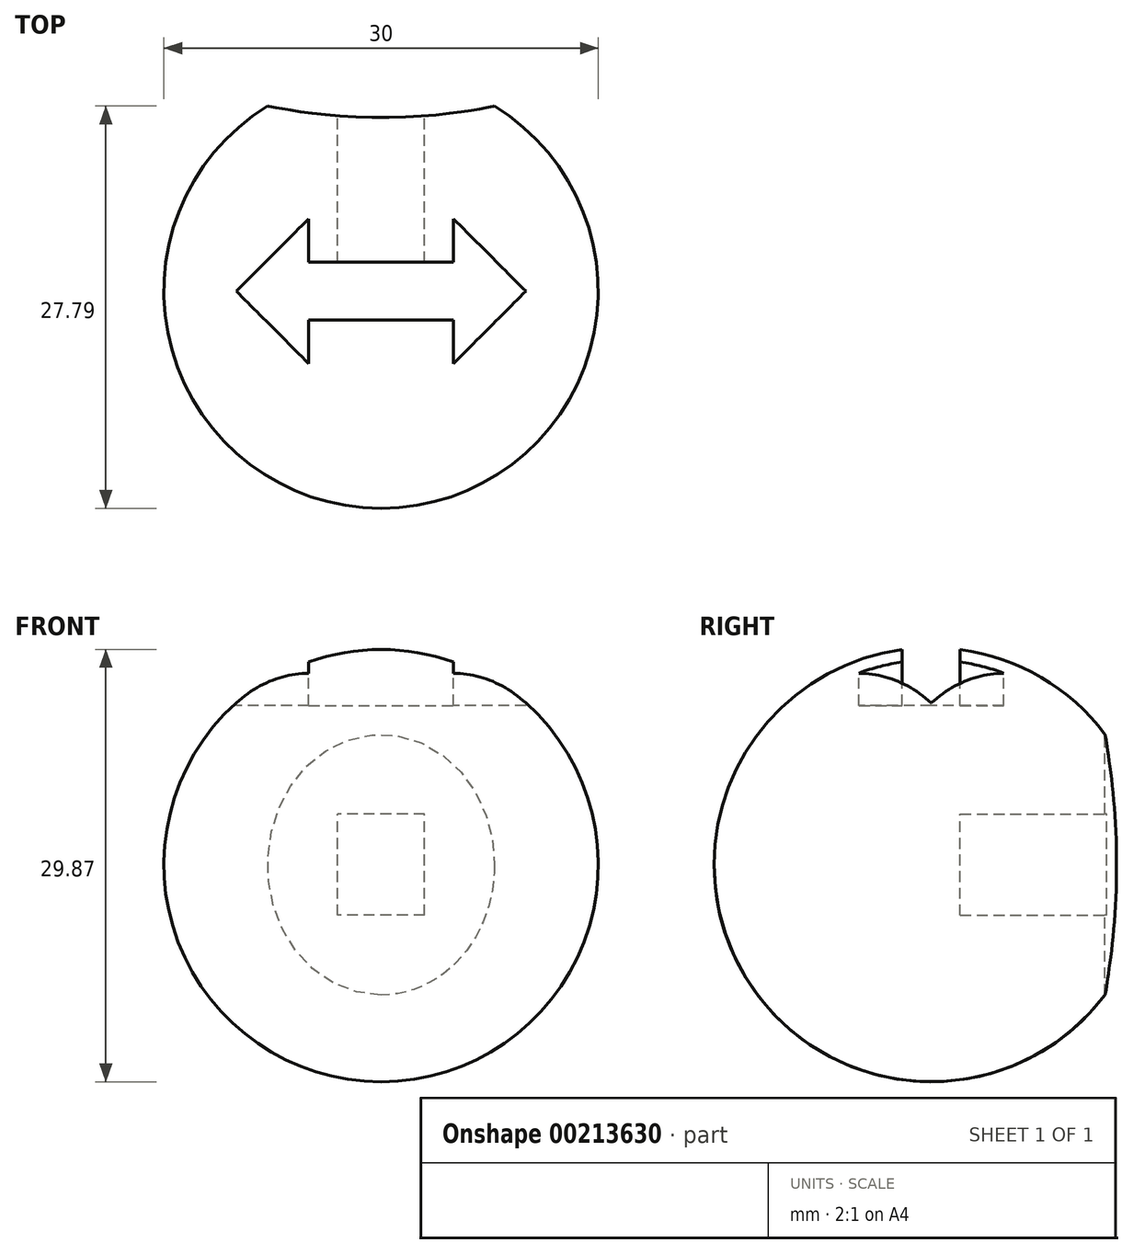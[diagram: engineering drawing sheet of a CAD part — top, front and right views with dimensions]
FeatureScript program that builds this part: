
annotation { "Feature Type Name" : "Feature", "Feature Type Description" : "" }
export const myFeature = defineFeature(function(context is Context, id is Id, definition is map)
    precondition{}
    {
        {
            var Q0;
            Q0=qCreatedBy(makeId("Right.planeOp"),FACE);
            var sketch = newSketch(context, id + "F0", { "sketchPlane" : qUnion([Q0])});
            skLineSegment(sketch, "E0", {"start": v(0, 0) * mm, "end": v(-30, 0) * mm});
            skArc(sketch, "E1", {"start": v(0, 0) * mm, "mid": v(-15, 15) * mm, "end": v(-30, 0) * mm});
            skSolve(sketch);
        }
        {
            var Q0;
            Q0=qSketchRegion(id+"F0",true);
            var Q1;
            Q1=sQuery(id+"F0.wireOp",EDGE,"E0");
            revolve(context, id + "F1", {"entities" : qUnion([Q0]), "axis" : qUnion([Q1]), "revolveType" : RevolveType.FULL});
        }
        {
            var Q0;
            Q0=qCreatedBy(makeId("Top.planeOp"),FACE);
            cPlane(context, id + "F2", {"entities" : qUnion([Q0]), "cplaneType" : CPlaneType.OFFSET, "offset" : 15 * mm, "width" : 150 * mm, "height" : 150 * mm});
        }
        {
            var Q0;
            Q0=qCreatedBy(id+"F2.planeOp",FACE);
            var sketch = newSketch(context, id + "F3", { "sketchPlane" : qUnion([Q0])});
            skLineSegment(sketch, "E2", {"start": v(0, 0) * mm, "end": v(0, -16.03) * mm, "construction": true});
            skLineSegment(sketch, "E3", {"start": v(0, 0) * mm, "end": v(-15, 0) * mm});
            skLineSegment(sketch, "E4", {"start": v(0, 0) * mm, "end": v(15, 0) * mm});
            skArc(sketch, "E5", {"start": v(-15, 0) * mm, "mid": v(0, -3) * mm, "end": v(15, 0) * mm});
            skSolve(sketch);
        }
        {
            var Q0;
            Q0=qSketchRegion(id+"F3",true);
            extrude(context, id + "F4", {"entities" : qUnion([Q0]), "operationType" : NewBodyOperationType.REMOVE, "endBound" : BoundingType.THROUGH_ALL, "oppositeDirection" : true, "depth" : 25 * mm});
        }
        {
            var Q0;
            Q0=qCreatedBy(makeId("Front.planeOp"),FACE);
            var sketch = newSketch(context, id + "F5", { "sketchPlane" : qUnion([Q0])});
            skLineSegment(sketch, "E6.bottom", {"start": v(3, -3.5) * mm, "end": v(-3, -3.5) * mm});
            skLineSegment(sketch, "E6.top", {"start": v(3, 3.5) * mm, "end": v(-3, 3.5) * mm});
            skLineSegment(sketch, "E6.left", {"start": v(3, -3.5) * mm, "end": v(3, 3.5) * mm});
            skLineSegment(sketch, "E6.right", {"start": v(-3, -3.5) * mm, "end": v(-3, 3.5) * mm});
            skPoint(sketch, "E6.middle", {"position": v(0, 0) * mm});
            skSolve(sketch);
        }
        {
            var Q0;
            Q0=qSketchRegion(id+"F5",true);
            extrude(context, id + "F6", {"entities" : qUnion([Q0]), "operationType" : NewBodyOperationType.REMOVE, "depth" : 13 * mm});
        }
        {
            var Q0;
            Q0=qCreatedBy(makeId("Top.planeOp"),FACE);
            cPlane(context, id + "F7", {"entities" : qUnion([Q0]), "cplaneType" : CPlaneType.OFFSET, "offset" : 18 * mm, "width" : 150 * mm, "height" : 150 * mm});
        }
        {
            var Q0;
            Q0=qCreatedBy(id+"F7.planeOp",FACE);
            var sketch = newSketch(context, id + "F8", { "sketchPlane" : qUnion([Q0])});
            skLineSegment(sketch, "E7", {"start": v(11.6, -15) * mm, "end": v(0, -15) * mm, "construction": true});
            skLineSegment(sketch, "E8", {"start": v(0, -15) * mm, "end": v(34.82, -15) * mm, "construction": true});
            skLineSegment(sketch, "E9.bottom", {"start": v(-5, -13) * mm, "end": v(5, -13) * mm});
            skLineSegment(sketch, "E9.top", {"start": v(-5, -17) * mm, "end": v(5, -17) * mm});
            skLineSegment(sketch, "E9.left", {"start": v(-5, -13) * mm, "end": v(-5, -17) * mm});
            skLineSegment(sketch, "E9.right", {"start": v(5, -13) * mm, "end": v(5, -17) * mm});
            skPoint(sketch, "E9.middle", {"position": v(0, -15) * mm});
            skLineSegment(sketch, "E10", {"start": v(5, -13) * mm, "end": v(5, -10) * mm});
            skLineSegment(sketch, "E11", {"start": v(5, -10) * mm, "end": v(10, -15) * mm});
            skLineSegment(sketch, "E12", {"start": v(10, -15) * mm, "end": v(5, -20) * mm});
            skLineSegment(sketch, "E13", {"start": v(5, -20) * mm, "end": v(5, -17) * mm});
            skLineSegment(sketch, "E14", {"start": v(0, -17) * mm, "end": v(0, -13) * mm, "construction": true});
            skLineSegment(sketch, "E15.MirrorCS", {"start": v(-5, -13) * mm, "end": v(-5, -10) * mm});
            skLineSegment(sketch, "E16.MirrorCS", {"start": v(-5, -10) * mm, "end": v(-10, -15) * mm});
            skLineSegment(sketch, "E17.MirrorCS", {"start": v(-10, -15) * mm, "end": v(-5, -20) * mm});
            skLineSegment(sketch, "E18.MirrorCS", {"start": v(-5, -20) * mm, "end": v(-5, -17) * mm});
            skSolve(sketch);
        }
        {
            var Q0;
            Q0=qSketchRegion(id+"F8",true);
            var Q1;
            Q1=makeQuery(id+"F1.opRevolve","SWEPT_FACE",FACE,{"disambiguationData":[OSD([sQuery(id+"F0.wireOp",EDGE,"E1")])]});
            extrude(context, id + "F9", {"entities" : qUnion([Q0]), "operationType" : NewBodyOperationType.REMOVE, "oppositeDirection" : true, "endBoundEntityFace" : qUnion([Q1]), "depth" : 7 * mm});
        }
    });
